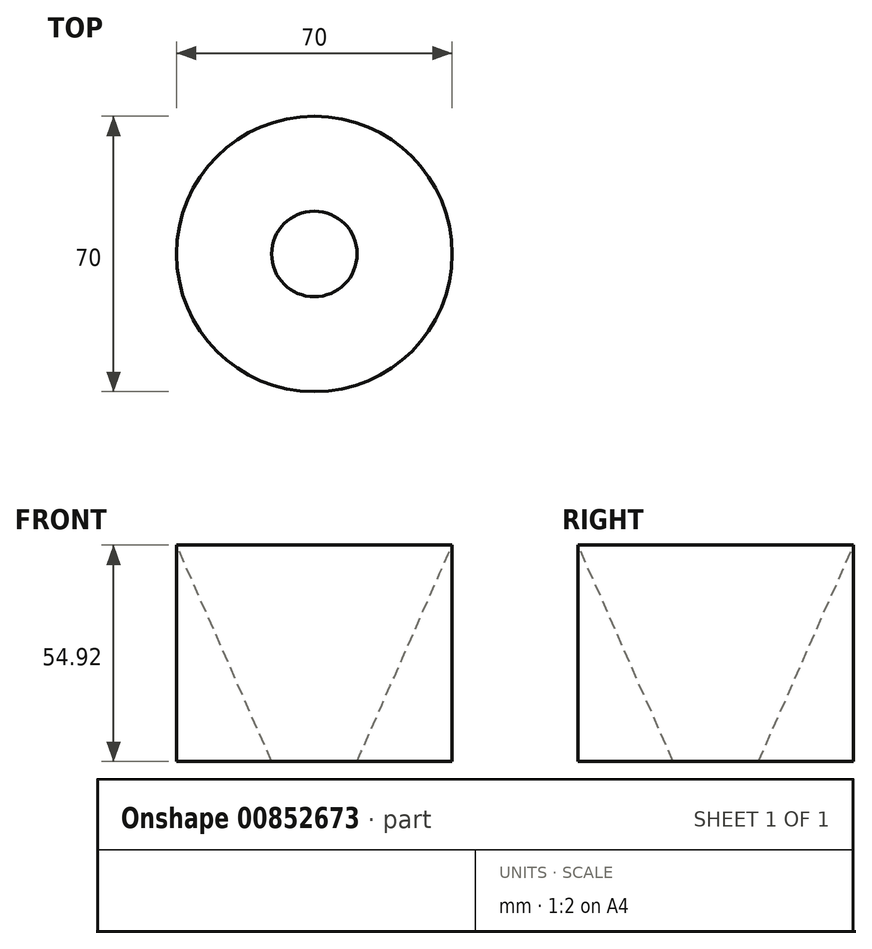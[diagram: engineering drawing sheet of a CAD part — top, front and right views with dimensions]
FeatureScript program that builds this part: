
annotation { "Feature Type Name" : "Feature", "Feature Type Description" : "" }
export const myFeature = defineFeature(function(context is Context, id is Id, definition is map)
    precondition{}
    {
        {
            var Q0;
            Q0=qCreatedBy(makeId("Front.planeOp"),FACE);
            var sketch = newSketch(context, id + "F0", { "sketchPlane" : qUnion([Q0])});
            skLineSegment(sketch, "E0", {"start": v(0, 102.9) * mm, "end": v(0, -117.07) * mm, "construction": true});
            skLineSegment(sketch, "E1", {"start": v(-10.86, 0) * mm, "end": v(-35, 0) * mm});
            skLineSegment(sketch, "E2", {"start": v(-35, 0) * mm, "end": v(-35, 54.92) * mm});
            skLineSegment(sketch, "E3", {"start": v(-35, 54.92) * mm, "end": v(-10.86, 0) * mm});
            skSolve(sketch);
        }
        {
            var Q0;
            Q0=makeQuery(id+"F0.imprint","IMPRINT",FACE,{"disambiguationData":[TD([[makeQuery(id+"F0.imprint","IMPRINT",EDGE,{"derivedFrom":sQuery(id+"F0.wireOp",EDGE,"E1")}),-1.0]])]});
            var Q1;
            Q1=sQuery(id+"F0.wireOp",EDGE,"E0");
            revolve(context, id + "F1", {"surfaceOperationType" : NewSurfaceOperationType.NEW, "entities" : qUnion([Q0]), "axis" : qUnion([Q1]), "revolveType" : RevolveType.FULL});
        }
    });
